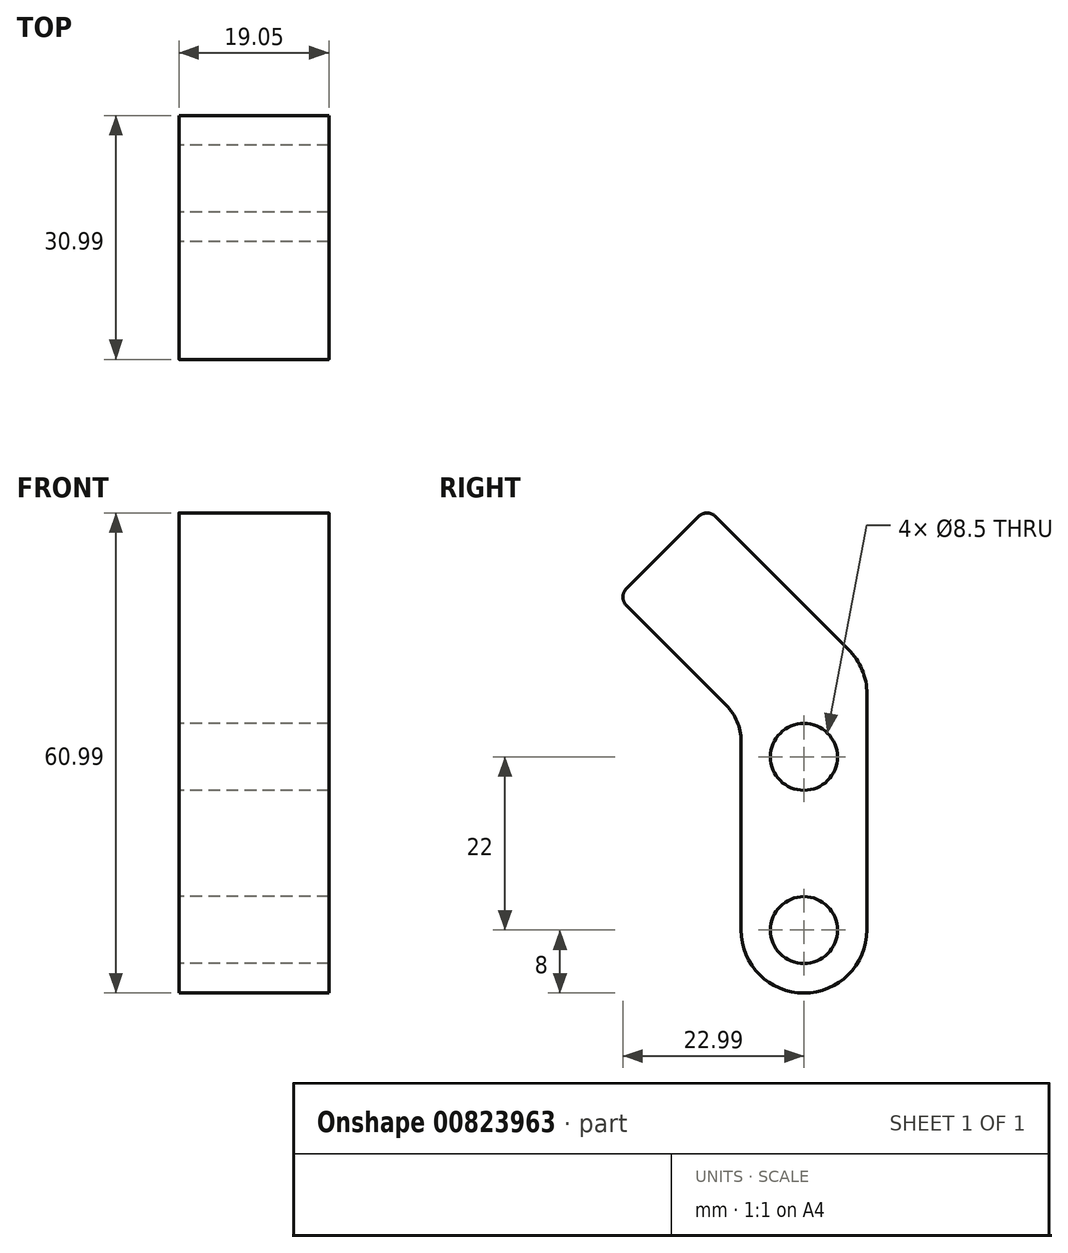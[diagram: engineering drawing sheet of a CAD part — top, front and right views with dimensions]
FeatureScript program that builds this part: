
annotation { "Feature Type Name" : "Feature", "Feature Type Description" : "" }
export const myFeature = defineFeature(function(context is Context, id is Id, definition is map)
    precondition{}
    {
        {
            var Q0;
            Q0=qCreatedBy(makeId("Right.planeOp"),FACE);
            var sketch = newSketch(context, id + "F0", { "sketchPlane" : qUnion([Q0])});
            skCircle(sketch, "E0", {"center": v(0, 0) * mm, "radius": 4.25 * mm});
            skCircle(sketch, "E1", {"center": v(0, 22) * mm, "radius": 4.25 * mm});
            skArc(sketch, "E2", {"start": v(-8, 0) * mm, "mid": v(0, -8) * mm, "end": v(8, 0) * mm});
            skArc(sketch, "E3", {"start": v(8, 30) * mm, "mid": v(7.4, 33.06) * mm, "end": v(5.66, 35.66) * mm});
            skLineSegment(sketch, "E4", {"start": v(8, 0) * mm, "end": v(8, 30) * mm});
            skLineSegment(sketch, "E5", {"start": v(5.66, 35.66) * mm, "end": v(-11.23, 52.54) * mm});
            skLineSegment(sketch, "E6", {"start": v(-13.38, 52.54) * mm, "end": v(-22.54, 43.38) * mm});
            skLineSegment(sketch, "E7", {"start": v(-9.86, 28.55) * mm, "end": v(-22.54, 41.23) * mm});
            skLineSegment(sketch, "E8", {"start": v(-8, 0) * mm, "end": v(-8, 24.06) * mm});
            skPoint(sketch, "E9.visualSharp", {"position": v(-8, 26.69) * mm});
            skArc(sketch, "E9.filletArc", {"start": v(-8, 24.06) * mm, "mid": v(-8.48, 26.49) * mm, "end": v(-9.86, 28.55) * mm});
            skLineSegment(sketch, "E10", {"start": v(-17.96, 36.65) * mm, "end": v(-6.65, 47.96) * mm, "construction": true});
            skPoint(sketch, "E11.visualSharp", {"position": v(-23.62, 42.3) * mm});
            skArc(sketch, "E11.filletArc", {"start": v(-22.54, 43.38) * mm, "mid": v(-22.99, 42.3) * mm, "end": v(-22.54, 41.23) * mm});
            skPoint(sketch, "E12.visualSharp", {"position": v(-12.3, 53.62) * mm});
            skArc(sketch, "E12.filletArc", {"start": v(-11.23, 52.54) * mm, "mid": v(-12.3, 52.99) * mm, "end": v(-13.38, 52.54) * mm});
            skSolve(sketch);
        }
        {
            var Q0;
            Q0=makeQuery(id+"F0.imprint","IMPRINT",FACE,{"disambiguationData":[TD([[makeQuery(id+"F0.imprint","IMPRINT",EDGE,{"derivedFrom":sQuery(id+"F0.wireOp",EDGE,"E0")}),-1.0]])]});
            extrude(context, id + "F1", {"entities" : qUnion([Q0]), "depth" : 19.05 * mm, "offsetDistance" : 25.4 * mm});
        }
    });
